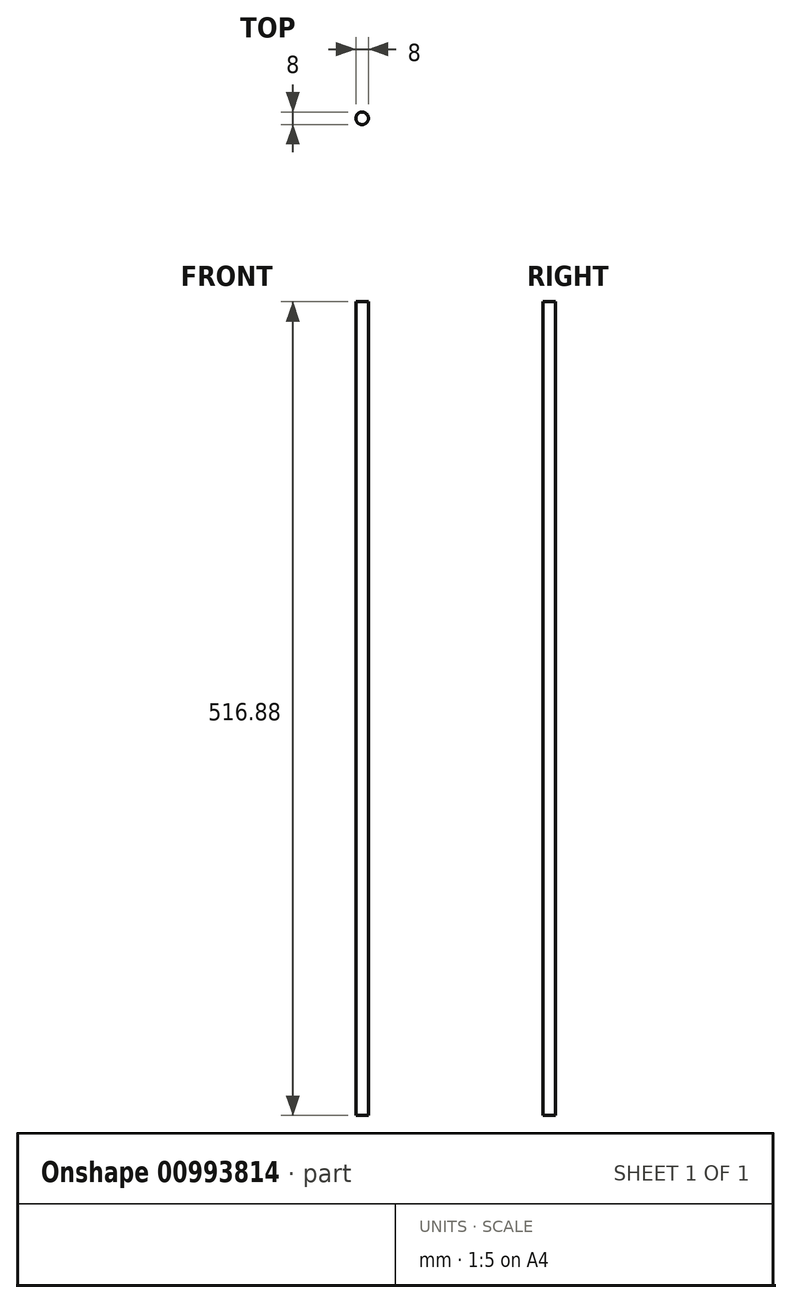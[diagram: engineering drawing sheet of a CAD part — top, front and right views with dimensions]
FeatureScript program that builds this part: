
annotation { "Feature Type Name" : "Feature", "Feature Type Description" : "" }
export const myFeature = defineFeature(function(context is Context, id is Id, definition is map)
    precondition{}
    {
        {
            var Q0;
            Q0=qCreatedBy(makeId("Top.planeOp"),FACE);
            var sketch = newSketch(context, id + "F0", { "sketchPlane" : qUnion([Q0])});
            skCircle(sketch, "E0", {"center": v(0, 0) * mm, "radius": 4 * mm});
            skSolve(sketch);
        }
        {
            var Q0;
            Q0 = qSketchRegion(id + "F0", true);
            extrude(context, id + "F1", {"entities" : qUnion([Q0]), "depth" : 516.88 * mm, "offsetDistance" : 25 * mm, "symmetric" : true});
        }
    });
